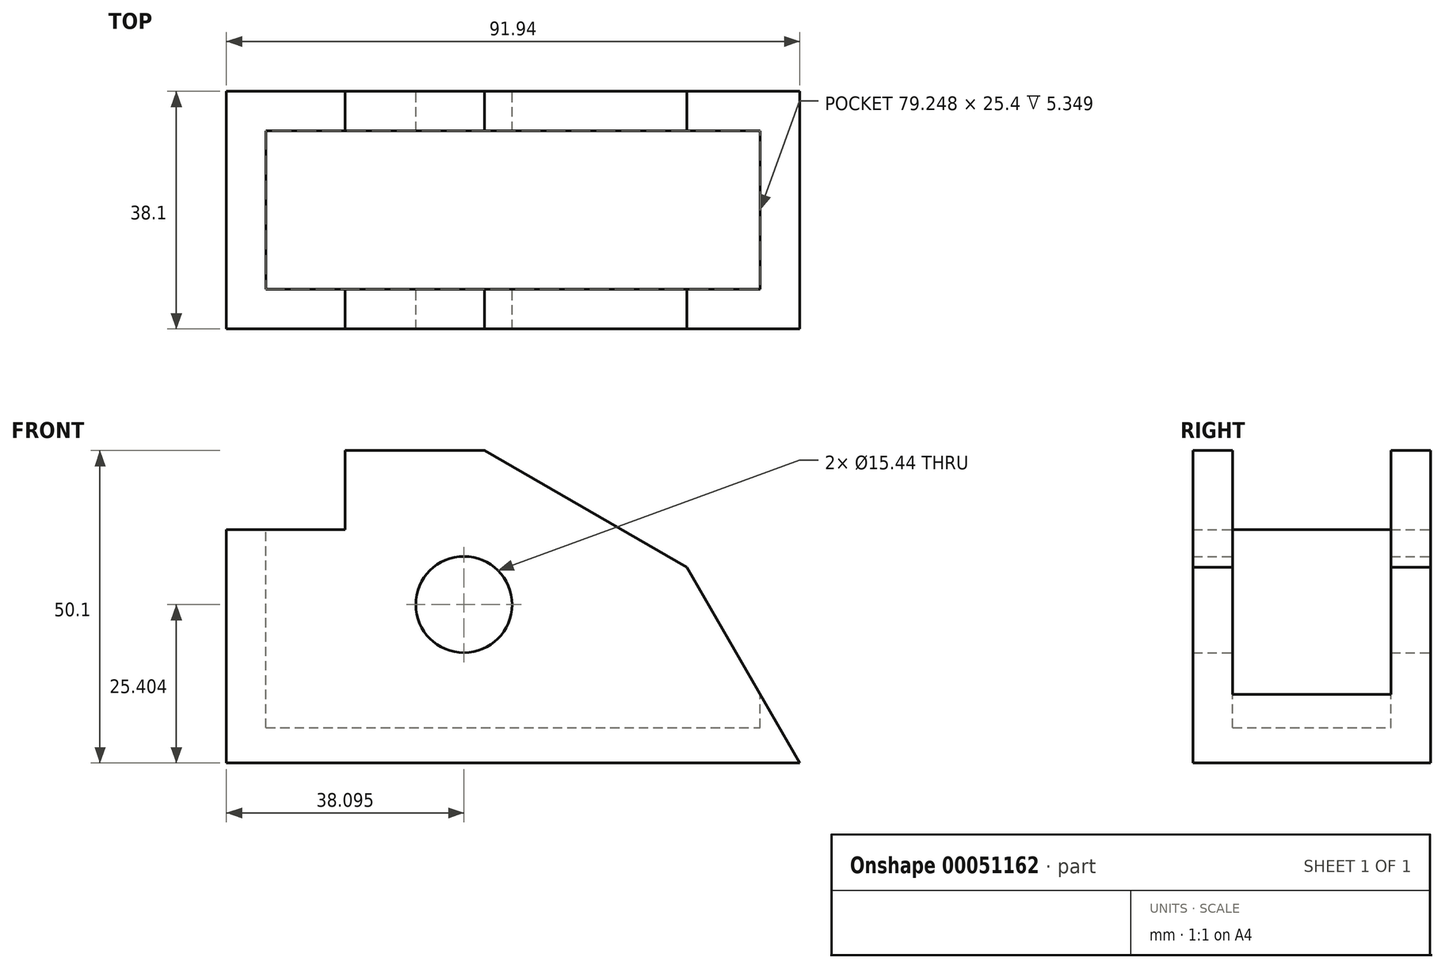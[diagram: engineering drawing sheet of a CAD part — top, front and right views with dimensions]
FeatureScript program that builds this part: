
annotation { "Feature Type Name" : "Feature", "Feature Type Description" : "" }
export const myFeature = defineFeature(function(context is Context, id is Id, definition is map)
    precondition{}
    {
        {
            var Q0;
            Q0=qCreatedBy(makeId("Front.planeOp"),FACE);
            var sketch = newSketch(context, id + "F0", { "sketchPlane" : qUnion([Q0])});
            skLineSegment(sketch, "E0.bottom", {"start": v(-35.95, 47.84) * mm, "end": v(36.94, 47.84) * mm});
            skLineSegment(sketch, "E0.top", {"start": v(-55, -2.26) * mm, "end": v(36.94, -2.26) * mm});
            skLineSegment(sketch, "E0.left", {"start": v(-55, 35.14) * mm, "end": v(-55, -2.26) * mm});
            skLineSegment(sketch, "E0.right", {"start": v(36.94, 47.84) * mm, "end": v(36.94, -2.26) * mm});
            skPoint(sketch, "E1", {"position": v(-55, 35.14) * mm});
            skPoint(sketch, "E2", {"position": v(-35.95, 47.84) * mm});
            skLineSegment(sketch, "E3", {"start": v(-55, 35.14) * mm, "end": v(-35.95, 35.14) * mm});
            skLineSegment(sketch, "E4", {"start": v(-35.95, 35.14) * mm, "end": v(-35.95, 47.84) * mm});
            skPoint(sketch, "E5.orphan", {"position": v(-55, 47.84) * mm});
            skPoint(sketch, "E6", {"position": v(-13.6, 47.84) * mm});
            skLineSegment(sketch, "E7", {"start": v(36.94, -2.26) * mm, "end": v(36.94, 47.84) * mm});
            skLineSegment(sketch, "E8", {"start": v(-13.6, 47.84) * mm, "end": v(18.83, 29.12) * mm});
            skLineSegment(sketch, "E9", {"start": v(36.94, -2.26) * mm, "end": v(-2.6, 66.25) * mm});
            skCircle(sketch, "E10", {"center": v(-16.9, 23.14) * mm, "radius": 7.72 * mm});
            skSolve(sketch);
        }
        {
            var Q0;
            {var subQ0=sQuery(id+"F0.wireOp",EDGE,"E0.top");Q0=makeQuery(id+"F0.imprint","IMPRINT",FACE,{"disambiguationData":[TD([[makeQuery(id+"F0.imprint","IMPRINT",EDGE,{"derivedFrom":subQ0}),1.0]])]});}
            extrude(context, id + "F1", {"entities" : qUnion([Q0]), "depth" : 38.1 * mm});
        }
        {
            var Q0;
            Q0=makeQuery(id+"F1.opExtrude","SWEPT_FACE",FACE,{"disambiguationData":[OSD([sQuery(id+"F0.wireOp",EDGE,"E3")])]});
            var sketch = newSketch(context, id + "F2", { "sketchPlane" : qUnion([Q0])});
            skLineSegment(sketch, "E11.bottom", {"start": v(-42.3, -6.35) * mm, "end": v(-48.65, -6.35) * mm});
            skLineSegment(sketch, "E11.top", {"start": v(-42.3, -11.75) * mm, "end": v(-48.65, -11.75) * mm});
            skLineSegment(sketch, "E11.left", {"start": v(-42.3, -6.35) * mm, "end": v(-42.3, -11.75) * mm});
            skLineSegment(sketch, "E11.right", {"start": v(-48.65, -6.35) * mm, "end": v(-48.65, -11.75) * mm});
            skLineSegment(sketch, "E12.bottom", {"start": v(-42.3, -27.94) * mm, "end": v(-48.65, -27.94) * mm});
            skLineSegment(sketch, "E12.top", {"start": v(-42.3, -31.75) * mm, "end": v(-48.65, -31.75) * mm});
            skLineSegment(sketch, "E12.left", {"start": v(-42.3, -27.94) * mm, "end": v(-42.3, -31.75) * mm});
            skLineSegment(sketch, "E12.right", {"start": v(-48.65, -27.94) * mm, "end": v(-48.65, -31.75) * mm});
            skSolve(sketch);
        }
        {
            var Q0;
            Q0=makeQuery(id+"F2.imprint","IMPRINT",FACE,{"disambiguationData":[TD([[makeQuery(id+"F2.imprint","IMPRINT",EDGE,{"derivedFrom":sQuery(id+"F2.wireOp",EDGE,"E12.bottom")}),1.0]])]});
            var Q1;
            Q1=makeQuery(id+"F2.imprint","IMPRINT",FACE,{"disambiguationData":[TD([[makeQuery(id+"F2.imprint","IMPRINT",EDGE,{"derivedFrom":sQuery(id+"F2.wireOp",EDGE,"E11.bottom")}),1.0]])]});
            extrude(context, id + "F3", {"entities" : qUnion([Q0, Q1]), "operationType" : NewBodyOperationType.ADD, "depth" : 12.7 * mm});
        }
        {
            var Q0;
            Q0=makeQuery(id+"F3.opExtrude","CAP_FACE",FACE,{"disambiguationData":[OSD([sQuery(id+"F2.wireOp",EDGE,"E12.bottom"),sQuery(id+"F2.wireOp",EDGE,"E12.top"),sQuery(id+"F2.wireOp",EDGE,"E12.left"),sQuery(id+"F2.wireOp",EDGE,"E12.right")])],"isStart":false});
            var sketch = newSketch(context, id + "F4", { "sketchPlane" : qUnion([Q0])});
            skLineSegment(sketch, "E13.bottom", {"start": v(-48.65, -31.75) * mm, "end": v(30.6, -31.75) * mm});
            skLineSegment(sketch, "E13.top", {"start": v(-48.65, -6.35) * mm, "end": v(30.6, -6.35) * mm});
            skLineSegment(sketch, "E13.left", {"start": v(-48.65, -31.75) * mm, "end": v(-48.65, -6.35) * mm});
            skLineSegment(sketch, "E13.right", {"start": v(30.6, -31.75) * mm, "end": v(30.6, -6.35) * mm});
            skSolve(sketch);
        }
        {
            var Q0;
            Q0 = qSketchRegion(id + "F4", true);
            var Q1;
            {var subQ2=sQuery(id+"F4.wireOp",EDGE,"E13.top");Q1=makeQuery(id+"F4.imprint","IMPRINT",FACE,{"disambiguationData":[TD([[makeQuery(id+"F4.imprint","IMPRINT",EDGE,{"derivedFrom":subQ2}),-1.0]])]});}
            extrude(context, id + "F5", {"entities" : qUnion([Q0, Q1]), "operationType" : NewBodyOperationType.REMOVE, "oppositeDirection" : true, "depth" : 44.45 * mm});
        }
    });
